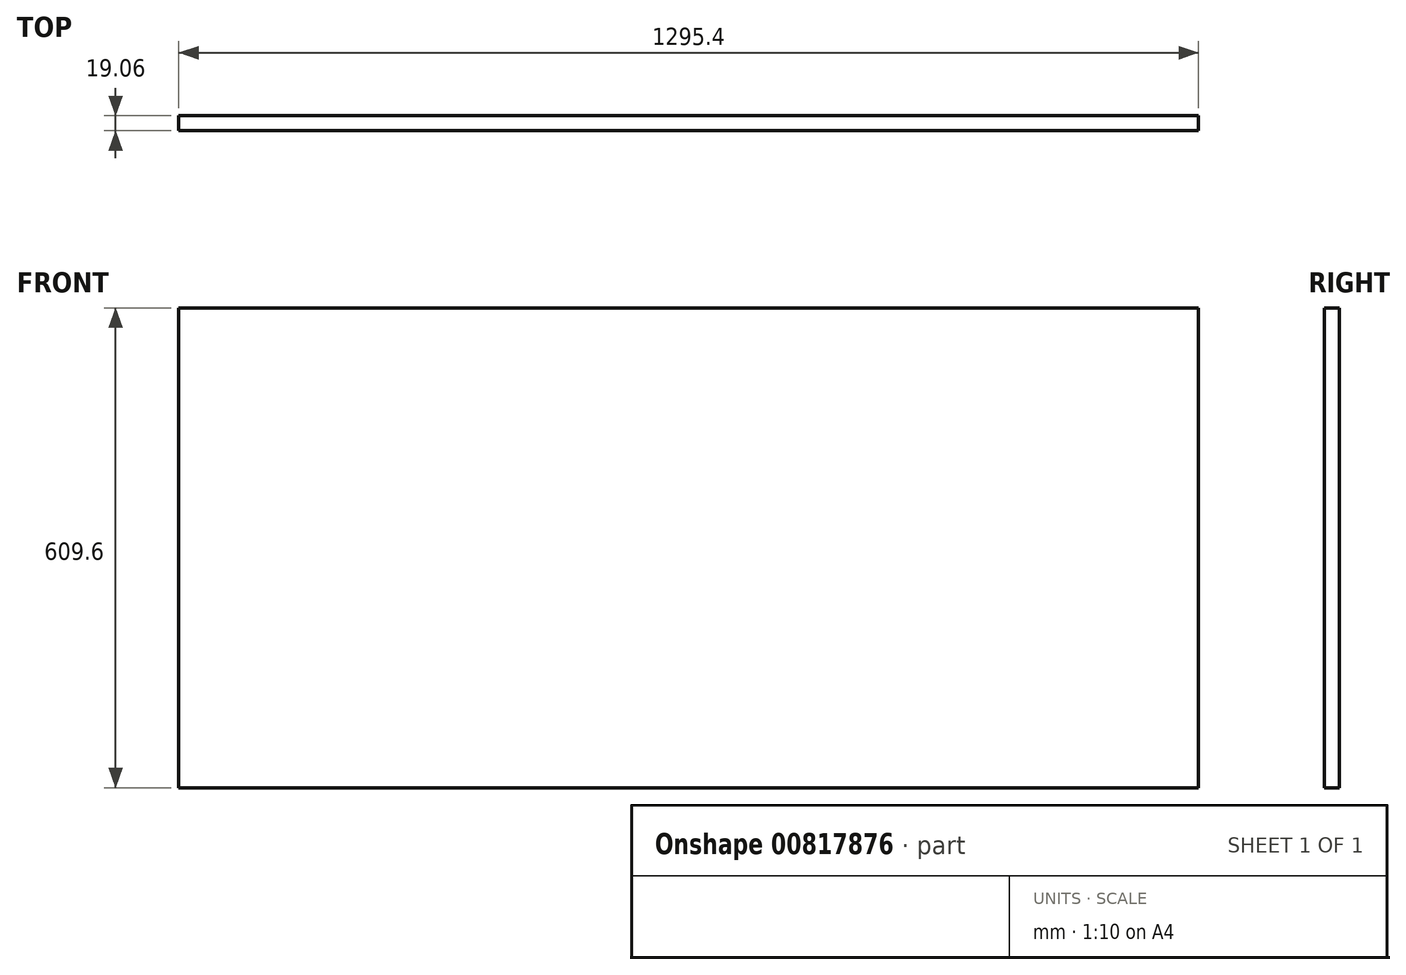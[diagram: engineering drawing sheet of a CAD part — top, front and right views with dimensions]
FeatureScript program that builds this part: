
annotation { "Feature Type Name" : "Feature", "Feature Type Description" : "" }
export const myFeature = defineFeature(function(context is Context, id is Id, definition is map)
    precondition{}
    {
        {
            var Q0;
            Q0=qCreatedBy(makeId("Front.planeOp"),FACE);
            var sketch = newSketch(context, id + "F0", { "sketchPlane" : qUnion([Q0])});
            skLineSegment(sketch, "E0.bottom", {"start": v(-646.04, -365.46) * mm, "end": v(649.36, -365.46) * mm});
            skLineSegment(sketch, "E0.top", {"start": v(-646.04, 244.14) * mm, "end": v(649.36, 244.14) * mm});
            skLineSegment(sketch, "E0.left", {"start": v(-646.04, -365.46) * mm, "end": v(-646.04, 244.14) * mm});
            skLineSegment(sketch, "E0.right", {"start": v(649.36, -365.46) * mm, "end": v(649.36, 244.14) * mm});
            skSolve(sketch);
        }
        {
            var Q0;
            Q0 = qSketchRegion(id + "F0", true);
            extrude(context, id + "F1", {"entities" : qUnion([Q0]), "endBound" : BoundingType.SYMMETRIC, "depth" : 19.05 * mm, "offsetDistance" : 25.4 * mm});
        }
    });
